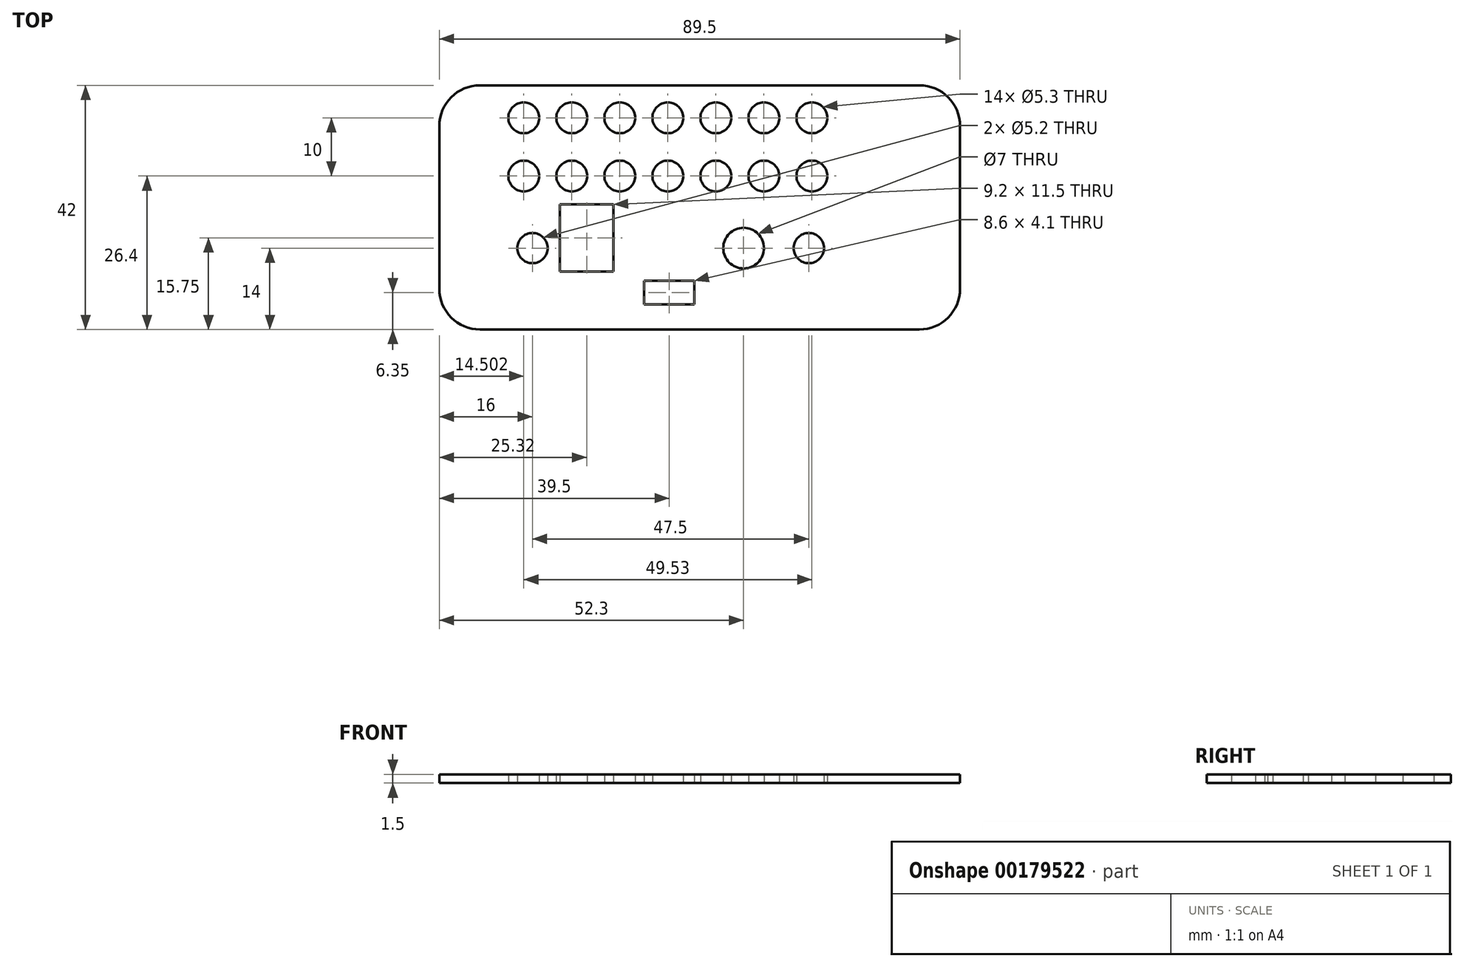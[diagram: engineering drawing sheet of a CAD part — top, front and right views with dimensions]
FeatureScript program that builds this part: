
annotation { "Feature Type Name" : "Feature", "Feature Type Description" : "" }
export const myFeature = defineFeature(function(context is Context, id is Id, definition is map)
    precondition{}
    {
        {
            var Q0;
            Q0=qCreatedBy(makeId("Top.planeOp"),FACE);
            var sketch = newSketch(context, id + "F0", { "sketchPlane" : qUnion([Q0])});
            skLineSegment(sketch, "E0.bottom", {"start": v(37.75, -21) * mm, "end": v(-37.75, -21) * mm});
            skLineSegment(sketch, "E0.top", {"start": v(37.75, 21) * mm, "end": v(-37.75, 21) * mm});
            skLineSegment(sketch, "E0.left", {"start": v(44.75, -14) * mm, "end": v(44.75, 14) * mm});
            skLineSegment(sketch, "E0.right", {"start": v(-44.75, -14) * mm, "end": v(-44.75, 14) * mm});
            skPoint(sketch, "E0.middle", {"position": v(0, 0) * mm});
            skPoint(sketch, "E1.visualSharp", {"position": v(-44.75, 21) * mm});
            skArc(sketch, "E1.filletArc", {"start": v(-37.75, 21) * mm, "mid": v(-42.7, 18.95) * mm, "end": v(-44.75, 14) * mm});
            skPoint(sketch, "E2.visualSharp", {"position": v(-44.75, -21) * mm});
            skArc(sketch, "E2.filletArc", {"start": v(-44.75, -14) * mm, "mid": v(-42.7, -18.95) * mm, "end": v(-37.75, -21) * mm});
            skPoint(sketch, "E3.visualSharp", {"position": v(44.75, 21) * mm});
            skArc(sketch, "E3.filletArc", {"start": v(44.75, 14) * mm, "mid": v(42.7, 18.95) * mm, "end": v(37.75, 21) * mm});
            skPoint(sketch, "E4.visualSharp", {"position": v(44.75, -21) * mm});
            skArc(sketch, "E4.filletArc", {"start": v(37.75, -21) * mm, "mid": v(42.7, -18.95) * mm, "end": v(44.75, -14) * mm});
            skLineSegment(sketch, "E5.bottom", {"start": v(-9.55, -12.6) * mm, "end": v(-0.95, -12.6) * mm});
            skLineSegment(sketch, "E5.top", {"start": v(-9.55, -16.7) * mm, "end": v(-0.95, -16.7) * mm});
            skLineSegment(sketch, "E5.left", {"start": v(-9.55, -12.6) * mm, "end": v(-9.55, -16.7) * mm});
            skLineSegment(sketch, "E5.right", {"start": v(-0.95, -12.6) * mm, "end": v(-0.95, -16.7) * mm});
            skPoint(sketch, "E6", {"position": v(7.55, -7) * mm});
            skPoint(sketch, "E7", {"position": v(18.75, -7) * mm});
            skPoint(sketch, "E8", {"position": v(-28.75, -7) * mm});
            skLineSegment(sketch, "E9.bottom", {"start": v(-24.03, 0.5) * mm, "end": v(-14.83, 0.5) * mm});
            skLineSegment(sketch, "E9.top", {"start": v(-24.03, -11) * mm, "end": v(-14.83, -11) * mm});
            skLineSegment(sketch, "E9.left", {"start": v(-24.03, 0.5) * mm, "end": v(-24.03, -11) * mm});
            skLineSegment(sketch, "E9.right", {"start": v(-14.83, 0.5) * mm, "end": v(-14.83, -11) * mm});
            skPoint(sketch, "E10", {"position": v(-30.25, 5.4) * mm});
            skPoint(sketch, "E11.0.1.0", {"position": v(-30.25, 15.4) * mm});
            skPoint(sketch, "E11.1.0.0", {"position": v(-22, 5.4) * mm});
            skPoint(sketch, "E11.1.1.0", {"position": v(-22, 15.4) * mm});
            skPoint(sketch, "E11.2.0.0", {"position": v(-13.74, 5.4) * mm});
            skPoint(sketch, "E11.2.1.0", {"position": v(-13.74, 15.4) * mm});
            skPoint(sketch, "E11.3.0.0", {"position": v(-5.48, 5.4) * mm});
            skPoint(sketch, "E11.3.1.0", {"position": v(-5.48, 15.4) * mm});
            skPoint(sketch, "E11.4.0.0", {"position": v(2.77, 5.4) * mm});
            skPoint(sketch, "E11.4.1.0", {"position": v(2.77, 15.4) * mm});
            skPoint(sketch, "E11.5.0.0", {"position": v(11.03, 5.4) * mm});
            skPoint(sketch, "E11.5.1.0", {"position": v(11.03, 15.4) * mm});
            skPoint(sketch, "E11.6.0.0", {"position": v(19.28, 5.4) * mm});
            skPoint(sketch, "E11.6.1.0", {"position": v(19.28, 15.4) * mm});
            skLineSegment(sketch, "E11.direction1", {"start": v(-30.25, 5.4) * mm, "end": v(-22, 5.4) * mm, "construction": true});
            skLineSegment(sketch, "E11.direction2", {"start": v(-30.25, 5.4) * mm, "end": v(-30.25, 15.4) * mm, "construction": true});
            skSolve(sketch);
        }
        {
            var Q0;
            Q0=makeQuery(id+"F0.imprint","IMPRINT",FACE,{"disambiguationData":[TD([[makeQuery(id+"F0.imprint","IMPRINT",EDGE,{"derivedFrom":sQuery(id+"F0.wireOp",EDGE,"E0.bottom")}),-1.0]])]});
            extrude(context, id + "F1", {"entities" : qUnion([Q0]), "depth" : 1.5 * mm});
        }
        {
            var Q0;
            Q0=sQuery(id+"F0.wireOp",VERTEX,"E7");
            var Q1;
            Q1=sQuery(id+"F0.wireOp",VERTEX,"E8");
            var Q2;
            Q2=makeQuery(id+"F1.opExtrude","SWEPT_BODY",BODY,{"disambiguationData":[OSD([sQuery(id+"F0.wireOp",EDGE,"E0.bottom"),sQuery(id+"F0.wireOp",EDGE,"E0.top"),sQuery(id+"F0.wireOp",EDGE,"E0.left"),sQuery(id+"F0.wireOp",EDGE,"E0.right"),sQuery(id+"F0.wireOp",EDGE,"E1.filletArc"),sQuery(id+"F0.wireOp",EDGE,"E2.filletArc"),sQuery(id+"F0.wireOp",EDGE,"E3.filletArc"),sQuery(id+"F0.wireOp",EDGE,"E4.filletArc"),sQuery(id+"F0.wireOp",EDGE,"E5.bottom"),sQuery(id+"F0.wireOp",EDGE,"E5.top"),sQuery(id+"F0.wireOp",EDGE,"E5.left"),sQuery(id+"F0.wireOp",EDGE,"E5.right"),sQuery(id+"F0.wireOp",EDGE,"E9.bottom"),sQuery(id+"F0.wireOp",EDGE,"E9.top"),sQuery(id+"F0.wireOp",EDGE,"E9.left"),sQuery(id+"F0.wireOp",EDGE,"E9.right")])]});
            hole(context, id + "F2", {"style" : HoleStyle.SIMPLE, "endStyle" : HoleEndStyle.BLIND, "oppositeDirection" : true, "holeDiameter" : 5.2 * mm, "holeDepth" : 2 * mm, "locations" : qUnion([Q0, Q1]), "scope" : qUnion([Q2])});
        }
        {
            var Q0;
            Q0=sQuery(id+"F0.wireOp",VERTEX,"E6");
            var Q1;
            Q1=makeQuery(id+"F1.opExtrude","SWEPT_BODY",BODY,{"disambiguationData":[OSD([sQuery(id+"F0.wireOp",EDGE,"E0.bottom"),sQuery(id+"F0.wireOp",EDGE,"E0.top"),sQuery(id+"F0.wireOp",EDGE,"E0.left"),sQuery(id+"F0.wireOp",EDGE,"E0.right"),sQuery(id+"F0.wireOp",EDGE,"E1.filletArc"),sQuery(id+"F0.wireOp",EDGE,"E2.filletArc"),sQuery(id+"F0.wireOp",EDGE,"E3.filletArc"),sQuery(id+"F0.wireOp",EDGE,"E4.filletArc"),sQuery(id+"F0.wireOp",EDGE,"E5.bottom"),sQuery(id+"F0.wireOp",EDGE,"E5.top"),sQuery(id+"F0.wireOp",EDGE,"E5.left"),sQuery(id+"F0.wireOp",EDGE,"E5.right"),sQuery(id+"F0.wireOp",EDGE,"E9.bottom"),sQuery(id+"F0.wireOp",EDGE,"E9.top"),sQuery(id+"F0.wireOp",EDGE,"E9.left"),sQuery(id+"F0.wireOp",EDGE,"E9.right")])]});
            hole(context, id + "F3", {"style" : HoleStyle.SIMPLE, "endStyle" : HoleEndStyle.BLIND, "oppositeDirection" : true, "holeDiameter" : 7 * mm, "holeDepth" : 2 * mm, "locations" : qUnion([Q0]), "scope" : qUnion([Q1])});
        }
        {
            var Q0;
            Q0=sQuery(id+"F0.wireOp",VERTEX,"E10");
            var Q1;
            Q1=sQuery(id+"F0.wireOp",VERTEX,"E11.0.1.0");
            var Q2;
            Q2=sQuery(id+"F0.wireOp",VERTEX,"E11.1.1.0");
            var Q3;
            Q3=sQuery(id+"F0.wireOp",VERTEX,"E11.1.0.0");
            var Q4;
            Q4=sQuery(id+"F0.wireOp",VERTEX,"E11.2.1.0");
            var Q5;
            Q5=sQuery(id+"F0.wireOp",VERTEX,"E11.2.0.0");
            var Q6;
            Q6=sQuery(id+"F0.wireOp",VERTEX,"E11.3.1.0");
            var Q7;
            Q7=sQuery(id+"F0.wireOp",VERTEX,"E11.3.0.0");
            var Q8;
            Q8=sQuery(id+"F0.wireOp",VERTEX,"E11.4.1.0");
            var Q9;
            Q9=sQuery(id+"F0.wireOp",VERTEX,"E11.4.0.0");
            var Q10;
            Q10=sQuery(id+"F0.wireOp",VERTEX,"E11.5.1.0");
            var Q11;
            Q11=sQuery(id+"F0.wireOp",VERTEX,"E11.5.0.0");
            var Q12;
            Q12=sQuery(id+"F0.wireOp",VERTEX,"E11.6.1.0");
            var Q13;
            Q13=sQuery(id+"F0.wireOp",VERTEX,"E11.6.0.0");
            var Q14;
            Q14=makeQuery(id+"F1.opExtrude","SWEPT_BODY",BODY,{"disambiguationData":[OSD([sQuery(id+"F0.wireOp",EDGE,"E0.bottom"),sQuery(id+"F0.wireOp",EDGE,"E0.top"),sQuery(id+"F0.wireOp",EDGE,"E0.left"),sQuery(id+"F0.wireOp",EDGE,"E0.right"),sQuery(id+"F0.wireOp",EDGE,"E1.filletArc"),sQuery(id+"F0.wireOp",EDGE,"E2.filletArc"),sQuery(id+"F0.wireOp",EDGE,"E3.filletArc"),sQuery(id+"F0.wireOp",EDGE,"E4.filletArc"),sQuery(id+"F0.wireOp",EDGE,"E5.bottom"),sQuery(id+"F0.wireOp",EDGE,"E5.top"),sQuery(id+"F0.wireOp",EDGE,"E5.left"),sQuery(id+"F0.wireOp",EDGE,"E5.right"),sQuery(id+"F0.wireOp",EDGE,"E9.bottom"),sQuery(id+"F0.wireOp",EDGE,"E9.top"),sQuery(id+"F0.wireOp",EDGE,"E9.left"),sQuery(id+"F0.wireOp",EDGE,"E9.right")])]});
            hole(context, id + "F4", {"style" : HoleStyle.SIMPLE, "endStyle" : HoleEndStyle.BLIND, "oppositeDirection" : true, "holeDiameter" : 5.3 * mm, "holeDepth" : 2 * mm, "locations" : qUnion([Q0, Q1, Q2, Q3, Q4, Q5, Q6, Q7, Q8, Q9, Q10, Q11, Q12, Q13]), "scope" : qUnion([Q14])});
        }
    });
